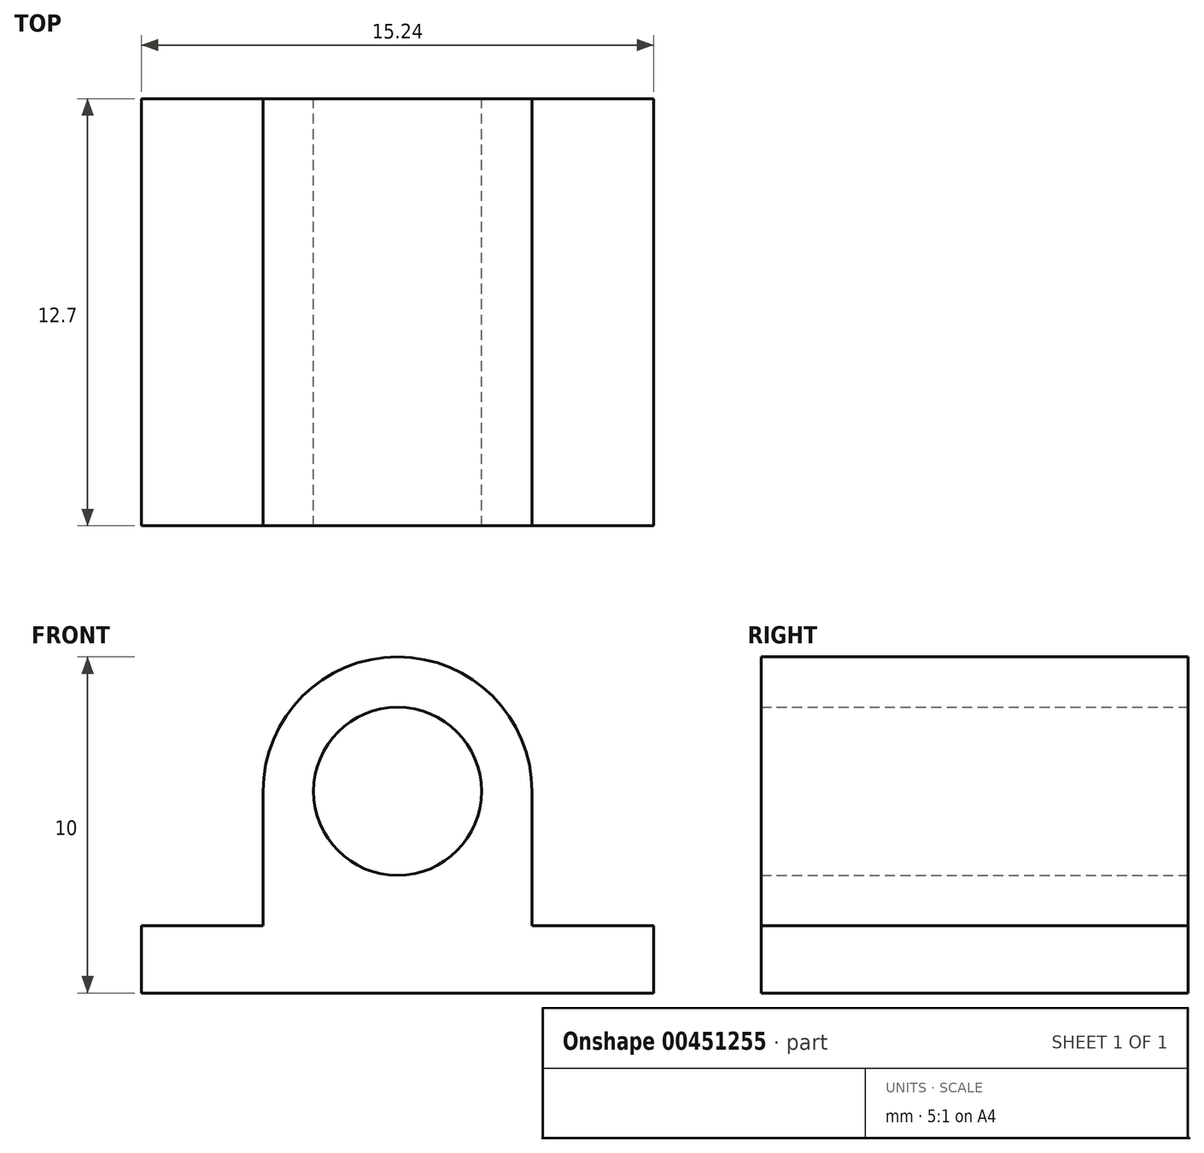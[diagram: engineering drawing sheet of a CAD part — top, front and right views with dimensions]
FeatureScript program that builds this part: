
annotation { "Feature Type Name" : "Feature", "Feature Type Description" : "" }
export const myFeature = defineFeature(function(context is Context, id is Id, definition is map)
    precondition{}
    {
        {
            var Q0;
            Q0=qCreatedBy(makeId("Front.planeOp"),FACE);
            var sketch = newSketch(context, id + "F0", { "sketchPlane" : qUnion([Q0])});
            skLineSegment(sketch, "E0", {"start": v(-7.62, 0) * mm, "end": v(-4, 0) * mm});
            skArc(sketch, "E1", {"start": v(4, 4) * mm, "mid": v(0, 8) * mm, "end": v(-4, 4) * mm});
            skCircle(sketch, "E2", {"center": v(0, 4) * mm, "radius": 2.5 * mm});
            skLineSegment(sketch, "E3", {"start": v(-4, 4) * mm, "end": v(-4, 0) * mm});
            skLineSegment(sketch, "E4", {"start": v(4, 4) * mm, "end": v(4, 0) * mm});
            skLineSegment(sketch, "E5.top", {"start": v(-7.62, -2) * mm, "end": v(7.62, -2) * mm});
            skLineSegment(sketch, "E5.left", {"start": v(-7.62, 0) * mm, "end": v(-7.62, -2) * mm});
            skLineSegment(sketch, "E5.right", {"start": v(7.62, 0) * mm, "end": v(7.62, -2) * mm});
            skLineSegment(sketch, "E6.trimOffspring", {"start": v(4, 0) * mm, "end": v(7.62, 0) * mm});
            skSolve(sketch);
        }
        {
            var Q0;
            Q0=makeQuery(id+"F0.imprint","IMPRINT",FACE,{"disambiguationData":[TD([[makeQuery(id+"F0.imprint","IMPRINT",EDGE,{"derivedFrom":sQuery(id+"F0.wireOp",EDGE,"E0")}),-1.0]])]});
            extrude(context, id + "F1", {"entities" : qUnion([Q0]), "depth" : 12.7 * mm});
        }
    });
